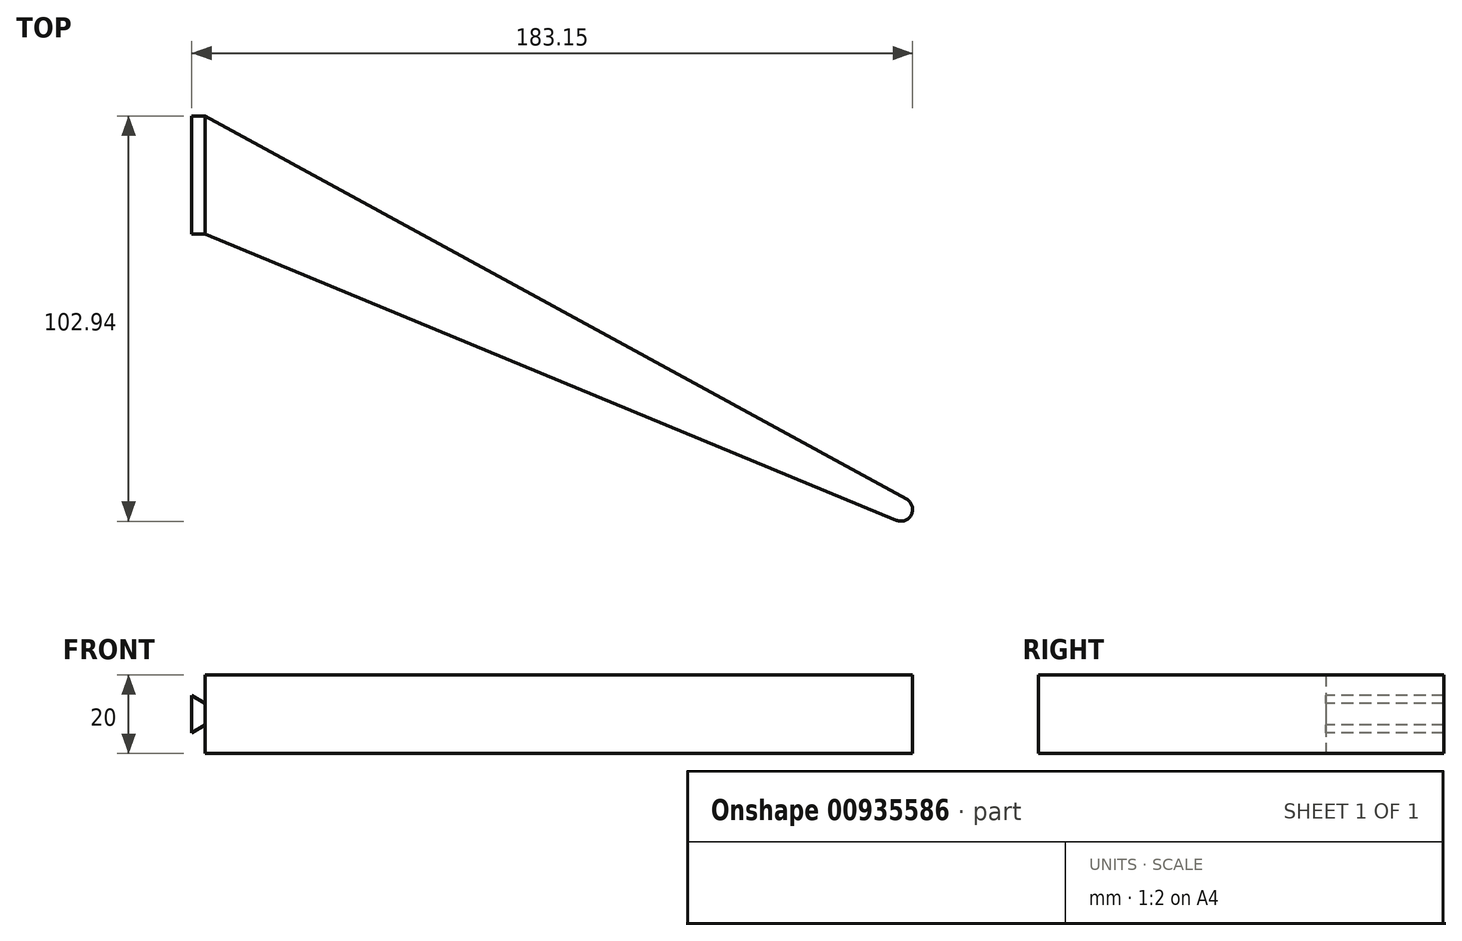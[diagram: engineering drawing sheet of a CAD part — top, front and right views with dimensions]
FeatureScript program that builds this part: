
annotation { "Feature Type Name" : "Feature", "Feature Type Description" : "" }
export const myFeature = defineFeature(function(context is Context, id is Id, definition is map)
    precondition{}
    {
        {
            var Q0;
            Q0=qCreatedBy(makeId("Top.planeOp"),FACE);
            var sketch = newSketch(context, id + "F0", { "sketchPlane" : qUnion([Q0])});
            skLineSegment(sketch, "E0", {"start": v(0, 0) * mm, "end": v(0, 30) * mm});
            skLineSegment(sketch, "E1", {"start": v(0, 0) * mm, "end": v(175.54, -72.7) * mm});
            skLineSegment(sketch, "E2", {"start": v(0, 30) * mm, "end": v(178.12, -67.3) * mm});
            skCircle(sketch, "E3", {"center": v(176.69, -69.94) * mm, "radius": 3 * mm});
            skSolve(sketch);
        }
        {
            var Q0;
            Q0 = qSketchRegion(id + "F0", true);
            extrude(context, id + "F1", {"entities" : qUnion([Q0]), "depth" : 20 * mm, "offsetDistance" : 25 * mm});
        }
        {
            var Q0;
            Q0=qCreatedBy(makeId("Front.planeOp"),FACE);
            var sketch = newSketch(context, id + "F2", { "sketchPlane" : qUnion([Q0])});
            skLineSegment(sketch, "E4", {"start": v(0, 12.75) * mm, "end": v(0, 7.25) * mm});
            skLineSegment(sketch, "E5", {"start": v(-3.46, 5.25) * mm, "end": v(0, 7.25) * mm});
            skLineSegment(sketch, "E6", {"start": v(0, 12.75) * mm, "end": v(-3.46, 14.75) * mm});
            skLineSegment(sketch, "E7", {"start": v(-3.46, 14.75) * mm, "end": v(-3.46, 5.25) * mm});
            skSolve(sketch);
        }
        {
            var Q0;
            Q0 = qSketchRegion(id + "F2", true);
            extrude(context, id + "F3", {"entities" : qUnion([Q0]), "operationType" : NewBodyOperationType.ADD, "oppositeDirection" : true, "depth" : 30 * mm, "offsetDistance" : 25 * mm});
        }
    });
